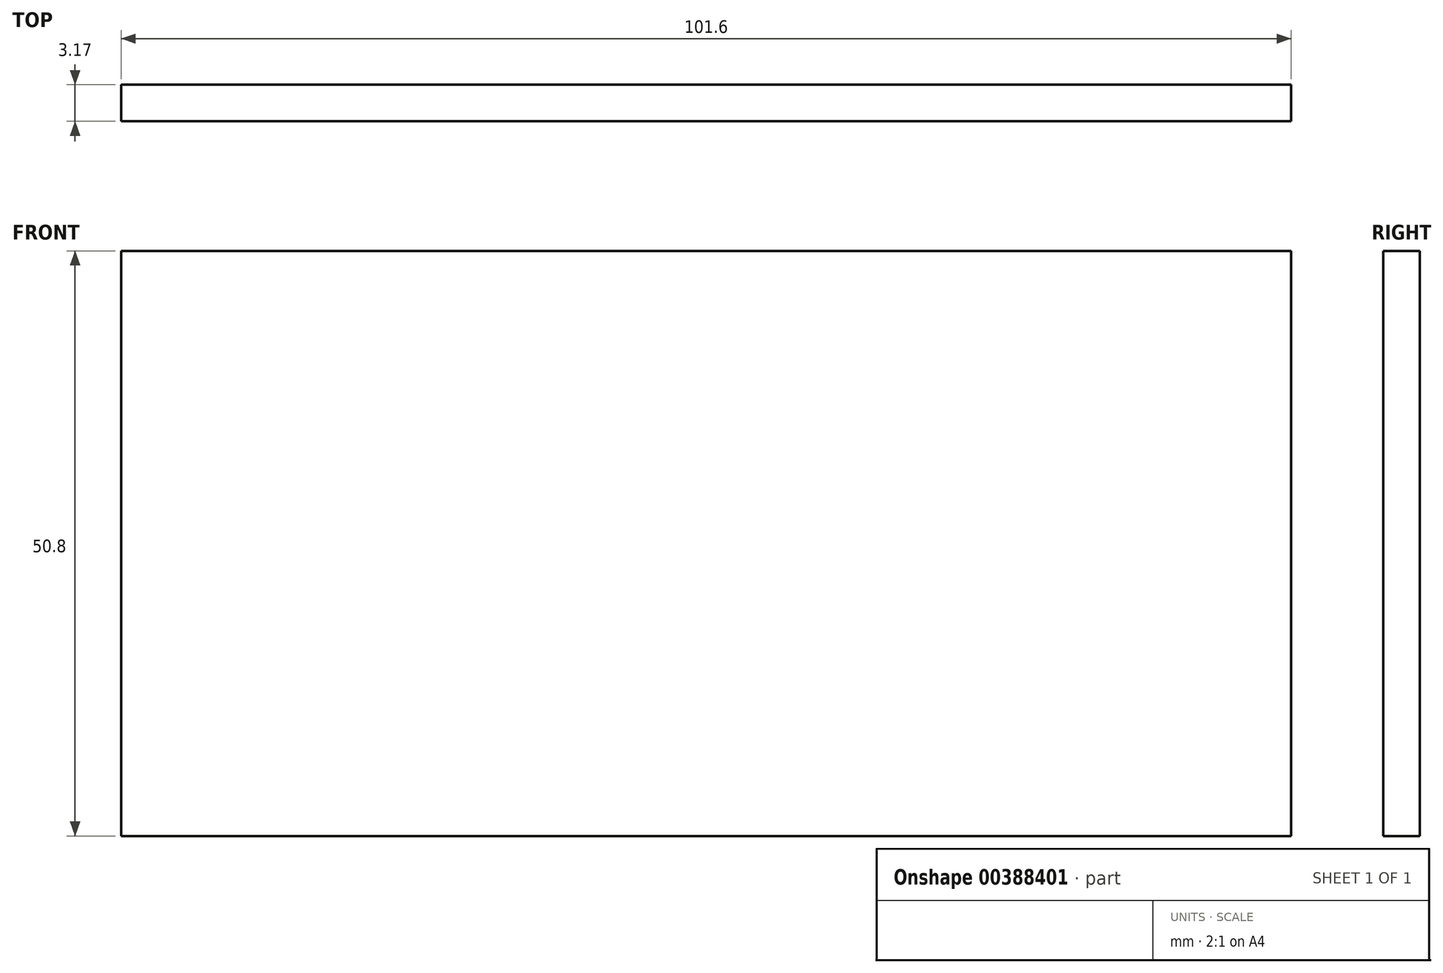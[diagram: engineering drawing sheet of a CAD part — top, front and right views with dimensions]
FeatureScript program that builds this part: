
annotation { "Feature Type Name" : "Feature", "Feature Type Description" : "" }
export const myFeature = defineFeature(function(context is Context, id is Id, definition is map)
    precondition{}
    {
        {
            var Q0;
            Q0=qCreatedBy(makeId("Front.planeOp"),FACE);
            var sketch = newSketch(context, id + "F0", { "sketchPlane" : qUnion([Q0])});
            skLineSegment(sketch, "E0.bottom", {"start": v(-52.27, 3.64) * mm, "end": v(49.33, 3.64) * mm});
            skLineSegment(sketch, "E0.top", {"start": v(-52.27, -47.16) * mm, "end": v(49.33, -47.16) * mm});
            skLineSegment(sketch, "E0.left", {"start": v(-52.27, 3.64) * mm, "end": v(-52.27, -47.16) * mm});
            skLineSegment(sketch, "E0.right", {"start": v(49.33, 3.64) * mm, "end": v(49.33, -47.16) * mm});
            skSolve(sketch);
        }
        {
            var Q0;
            Q0=makeQuery(id+"F0.imprint","IMPRINT",FACE,{"disambiguationData":[TD([[makeQuery(id+"F0.imprint","IMPRINT",EDGE,{"derivedFrom":sQuery(id+"F0.wireOp",EDGE,"E0.bottom")}),-1.0]])]});
            extrude(context, id + "F1", {"entities" : qUnion([Q0]), "depth" : 3.17 * mm});
        }
    });
